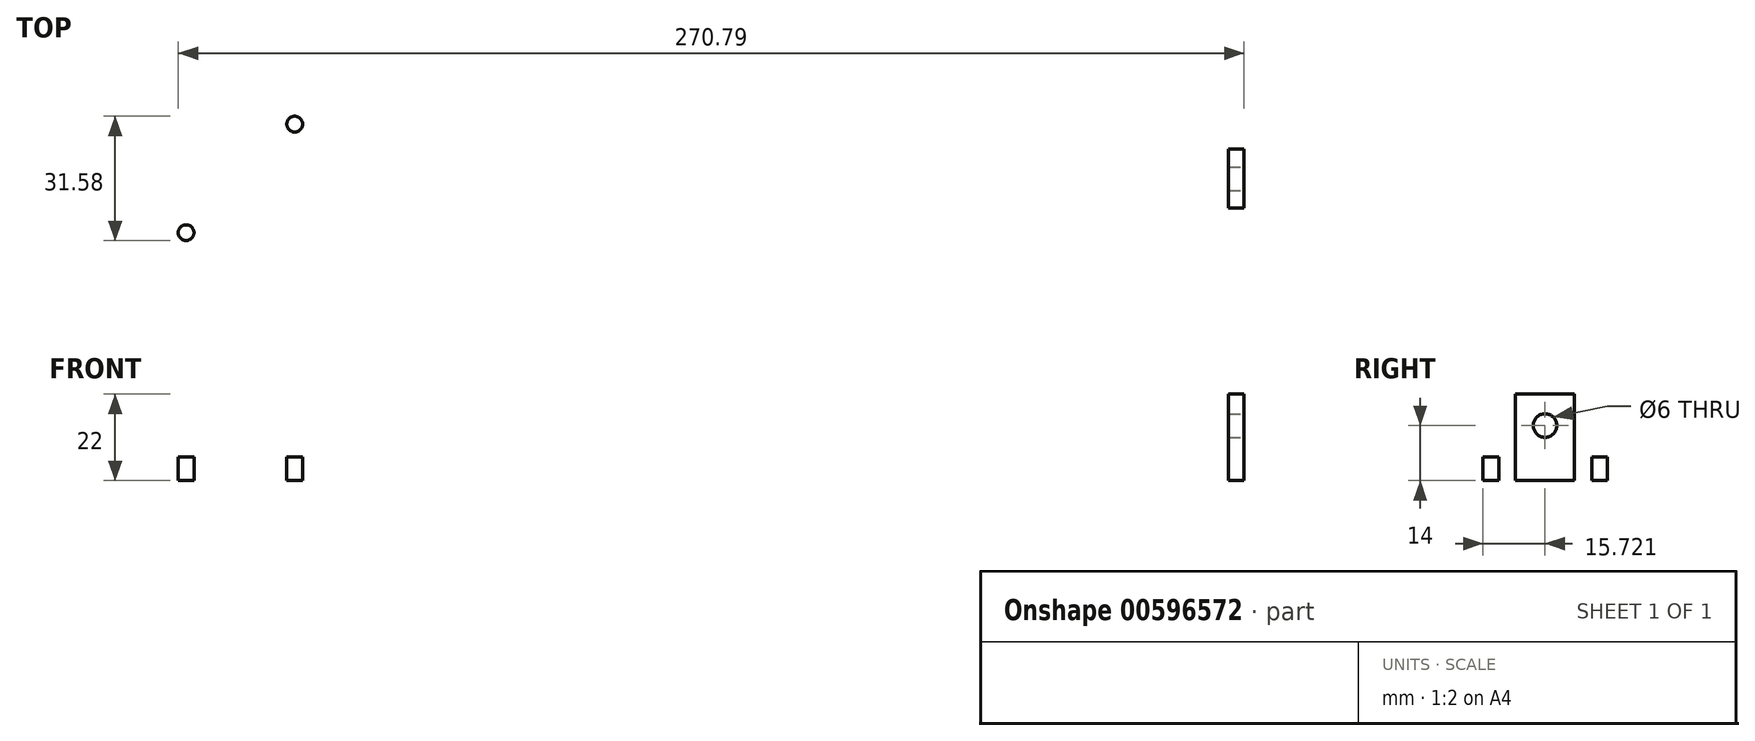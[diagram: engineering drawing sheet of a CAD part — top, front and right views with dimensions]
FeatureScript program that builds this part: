
annotation { "Feature Type Name" : "Feature", "Feature Type Description" : "" }
export const myFeature = defineFeature(function(context is Context, id is Id, definition is map)
    precondition{}
    {
        {
            var Q0;
            Q0=qCreatedBy(makeId("Top.planeOp"),FACE);
            var sketch = newSketch(context, id + "F0", { "sketchPlane" : qUnion([Q0])});
            skLineSegment(sketch, "E0", {"start": v(110, 35) * mm, "end": v(-110, 35) * mm});
            skArc(sketch, "E1", {"start": v(136.46, -35) * mm, "mid": v(147.42, 9.14) * mm, "end": v(110, 35) * mm});
            skLineSegment(sketch, "E2", {"start": v(132, 1) * mm, "end": v(88, 1) * mm});
            skArc(sketch, "E3", {"start": v(88, 1) * mm, "mid": v(82, -5) * mm, "end": v(88, -11) * mm});
            skLineSegment(sketch, "E4", {"start": v(88, -11) * mm, "end": v(131.86, -11) * mm});
            skArc(sketch, "E5", {"start": v(131.86, -11) * mm, "mid": v(138, -5.07) * mm, "end": v(132, 1) * mm});
            skArc(sketch, "E6", {"start": v(-110, 35) * mm, "mid": v(-147.42, 9.14) * mm, "end": v(-136.46, -35) * mm});
            skLineSegment(sketch, "E7", {"start": v(136.46, -35) * mm, "end": v(-136.46, -35) * mm});
            skCircle(sketch, "E8", {"center": v(40, 12) * mm, "radius": 3.25 * mm});
            skCircle(sketch, "E9", {"center": v(-40, -18) * mm, "radius": 3.25 * mm});
            skLineSegment(sketch, "E10", {"start": v(-75, 35) * mm, "end": v(75, 35) * mm});
            skLineSegment(sketch, "E11", {"start": v(75, -35) * mm, "end": v(-75, -35) * mm});
            skCircle(sketch, "E12", {"center": v(-110, -5) * mm, "radius": 16 * mm});
            skSolve(sketch);
        }
        {
            var Q0;
            {var subQ3=sQuery(id+"F0.wireOp",EDGE,"E1");Q0=makeQuery(id+"F0.imprint","IMPRINT",FACE,{"disambiguationData":[TD([[makeQuery(id+"F0.imprint","IMPRINT",EDGE,{"derivedFrom":subQ3}),1.0]])]});}
            extrude(context, id + "F1", {"entities" : qUnion([Q0]), "depth" : 6 * mm, "offsetDistance" : 25 * mm});
        }
        {
            var Q0;
            Q0=makeQuery(id+"F1.opExtrude","CAP_FACE",FACE,{"disambiguationData":[OSD([sQuery(id+"F0.wireOp",EDGE,"E0"),sQuery(id+"F0.wireOp",EDGE,"E1"),sQuery(id+"F0.wireOp",EDGE,"E2"),sQuery(id+"F0.wireOp",EDGE,"E3"),sQuery(id+"F0.wireOp",EDGE,"E4"),sQuery(id+"F0.wireOp",EDGE,"E5"),sQuery(id+"F0.wireOp",EDGE,"E6"),sQuery(id+"F0.wireOp",EDGE,"E7"),sQuery(id+"F0.wireOp",EDGE,"E9"),sQuery(id+"F0.wireOp",EDGE,"E10"),sQuery(id+"F0.wireOp",EDGE,"E11"),sQuery(id+"F0.wireOp",EDGE,"E8"),sQuery(id+"F0.wireOp",EDGE,"xTUdDgbX-3oi2-VUzh-4qs4-iaq1XoPYDxqc")])],"isStart":false});
            var sketch = newSketch(context, id + "F2", { "sketchPlane" : qUnion([Q0])});
            skLineSegment(sketch, "E13.bottom", {"start": v(141, 2.43) * mm, "end": v(145, 2.43) * mm});
            skLineSegment(sketch, "E13.top", {"start": v(141, -12.57) * mm, "end": v(145, -12.57) * mm});
            skLineSegment(sketch, "E13.left", {"start": v(141, 2.43) * mm, "end": v(141, -12.57) * mm});
            skLineSegment(sketch, "E13.right", {"start": v(145, 2.43) * mm, "end": v(145, -12.57) * mm});
            skSolve(sketch);
        }
        {
            var Q0;
            Q0=makeQuery(id+"F2.imprint","IMPRINT",FACE,{"disambiguationData":[TD([[makeQuery(id+"F2.imprint","IMPRINT",EDGE,{"derivedFrom":sQuery(id+"F2.wireOp",EDGE,"E13.bottom")}),-1.0]])]});
            extrude(context, id + "F3", {"entities" : qUnion([Q0]), "operationType" : NewBodyOperationType.ADD, "depth" : 16 * mm, "offsetDistance" : 25 * mm});
        }
        {
            var Q0;
            Q0=makeQuery(id+"F3.opExtrude","SWEPT_FACE",FACE,{"disambiguationData":[OSD([sQuery(id+"F2.wireOp",EDGE,"E13.right")])]});
            var sketch = newSketch(context, id + "F4", { "sketchPlane" : qUnion([Q0])});
            skCircle(sketch, "E14", {"center": v(-5.07, 14) * mm, "radius": 3 * mm});
            skPoint(sketch, "E14.centerSnap0", {"position": v(-5.07, 22) * mm});
            skSolve(sketch);
        }
        {
            var Q0;
            Q0=makeQuery(id+"F4.imprint","IMPRINT",FACE,{"disambiguationData":[TD([[makeQuery(id+"F4.imprint","IMPRINT",EDGE,{"derivedFrom":sQuery(id+"F4.wireOp",EDGE,"E14")}),1.0]])]});
            extrude(context, id + "F5", {"entities" : qUnion([Q0]), "operationType" : NewBodyOperationType.REMOVE, "oppositeDirection" : true, "depth" : 25 * mm, "offsetDistance" : 25 * mm});
        }
        {
            var Q0;
            Q0=makeQuery(id+"F1.opExtrude","CAP_FACE",FACE,{"disambiguationData":[OSD([sQuery(id+"F0.wireOp",EDGE,"E0"),sQuery(id+"F0.wireOp",EDGE,"E1"),sQuery(id+"F0.wireOp",EDGE,"E2"),sQuery(id+"F0.wireOp",EDGE,"E3"),sQuery(id+"F0.wireOp",EDGE,"E4"),sQuery(id+"F0.wireOp",EDGE,"E5"),sQuery(id+"F0.wireOp",EDGE,"E6"),sQuery(id+"F0.wireOp",EDGE,"E7"),sQuery(id+"F0.wireOp",EDGE,"E9"),sQuery(id+"F0.wireOp",EDGE,"E10"),sQuery(id+"F0.wireOp",EDGE,"E11"),sQuery(id+"F0.wireOp",EDGE,"E8"),sQuery(id+"F0.wireOp",EDGE,"E12")])],"isStart":false});
            var sketch = newSketch(context, id + "F6", { "sketchPlane" : qUnion([Q0])});
            skCircle(sketch, "E15", {"center": v(-110, -5) * mm, "radius": 19.5 * mm, "construction": true});
            skLineSegment(sketch, "E16", {"start": v(-110, -5) * mm, "end": v(-123.79, 8.79) * mm, "construction": true});
            skLineSegment(sketch, "E17", {"start": v(-110, -5) * mm, "end": v(-110, 0.98) * mm, "construction": true});
            skLineSegment(sketch, "E18", {"start": v(-110, -5) * mm, "end": v(-104.94, -5) * mm, "construction": true});
            skCircle(sketch, "E19", {"center": v(-123.79, 8.79) * mm, "radius": 2 * mm});
            skCircle(sketch, "E20.MirrorC", {"center": v(-96.21, 8.79) * mm, "radius": 2 * mm});
            skCircle(sketch, "E21.MirrorC", {"center": v(-96.21, -18.79) * mm, "radius": 2 * mm});
            skCircle(sketch, "E22.MirrorC", {"center": v(-123.79, -18.79) * mm, "radius": 2 * mm});
            skSolve(sketch);
        }
        {
            var Q0;
            Q0=makeQuery(id+"F6.imprint","IMPRINT",FACE,{"disambiguationData":[TD([[makeQuery(id+"F6.imprint","IMPRINT",EDGE,{"derivedFrom":sQuery(id+"F6.wireOp",EDGE,"E19")}),1.0]])]});
            var Q1;
            Q1=makeQuery(id+"F6.imprint","IMPRINT",FACE,{"disambiguationData":[TD([[makeQuery(id+"F6.imprint","IMPRINT",EDGE,{"derivedFrom":sQuery(id+"F6.wireOp",EDGE,"E20.MirrorC")}),-1.0]])]});
            var Q2;
            Q2=makeQuery(id+"F6.imprint","IMPRINT",FACE,{"disambiguationData":[TD([[makeQuery(id+"F6.imprint","IMPRINT",EDGE,{"derivedFrom":sQuery(id+"F6.wireOp",EDGE,"E21.MirrorC")}),1.0]])]});
            var Q3;
            Q3=makeQuery(id+"F6.imprint","IMPRINT",FACE,{"disambiguationData":[TD([[makeQuery(id+"F6.imprint","IMPRINT",EDGE,{"derivedFrom":sQuery(id+"F6.wireOp",EDGE,"E22.MirrorC")}),-1.0]])]});
            var Q4;
            Q4=makeQuery(id+"F6.imprint","IMPRINT",FACE,{"disambiguationData":[TD([[makeQuery(id+"F6.imprint","IMPRINT",EDGE,{"derivedFrom":makeQuery(id+"F1.opExtrude","CAP_EDGE",EDGE,{"disambiguationData":[OSD([sQuery(id+"F0.wireOp",EDGE,"E12")])],"isStart":false})}),1.0]])]});
            extrude(context, id + "F7", {"entities" : qUnion([Q0, Q1, Q2, Q3, Q4]), "operationType" : NewBodyOperationType.REMOVE, "oppositeDirection" : true, "depth" : 25 * mm, "offsetDistance" : 25 * mm});
        }
    });
